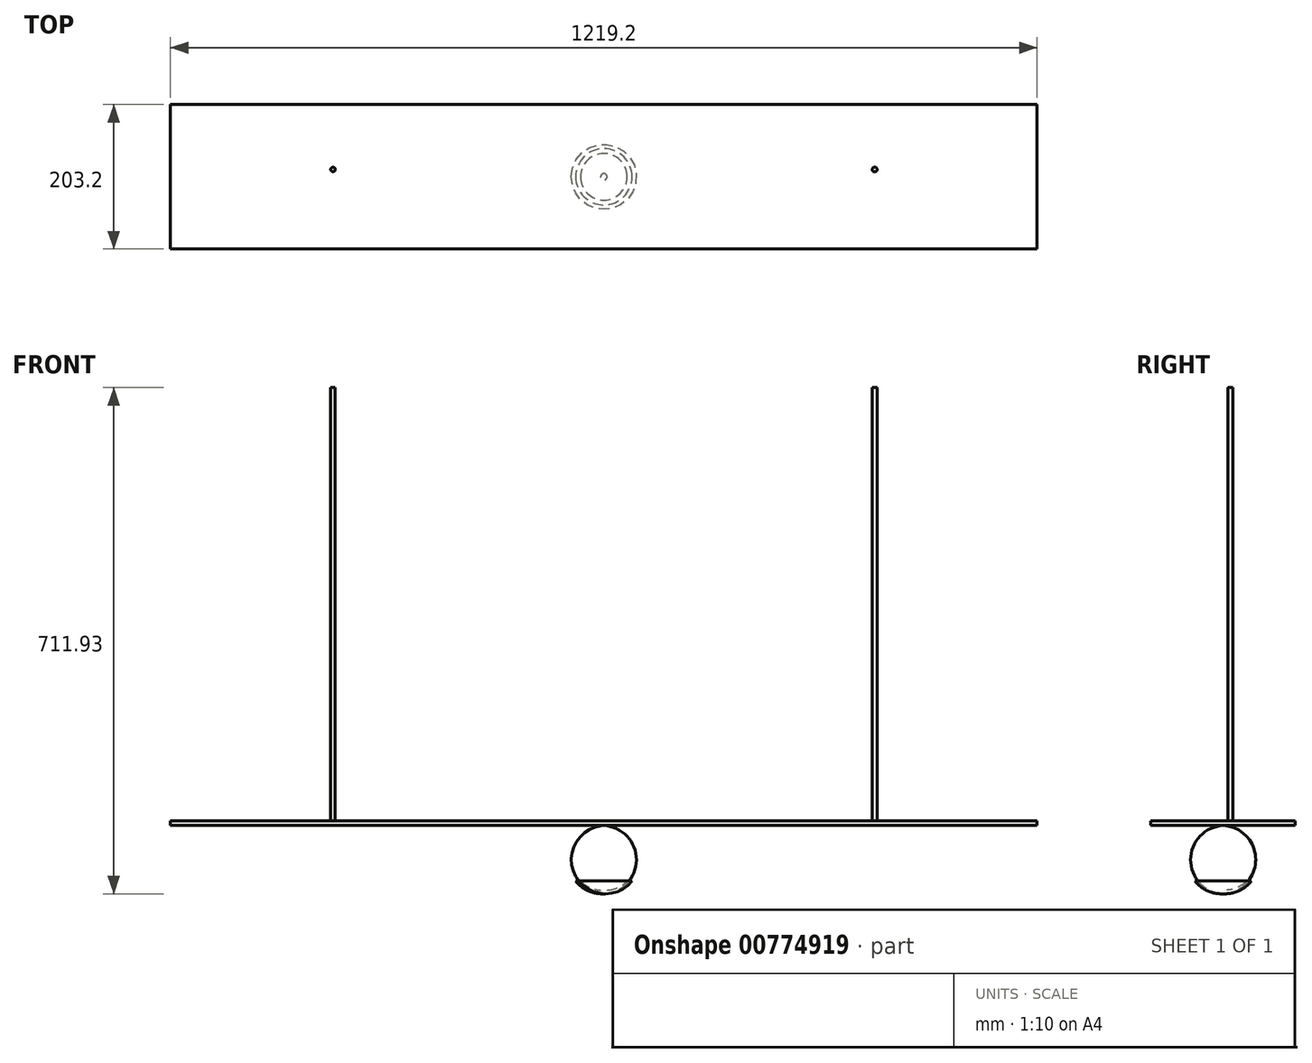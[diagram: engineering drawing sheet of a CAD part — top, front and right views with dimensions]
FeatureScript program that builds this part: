
annotation { "Feature Type Name" : "Feature", "Feature Type Description" : "" }
export const myFeature = defineFeature(function(context is Context, id is Id, definition is map)
    precondition{}
    {
        {
            var Q0;
            Q0=qCreatedBy(makeId("Top.planeOp"),FACE);
            var sketch = newSketch(context, id + "F0", { "sketchPlane" : qUnion([Q0])});
            skLineSegment(sketch, "E0.bottom", {"start": v(609.6, -101.6) * mm, "end": v(-609.6, -101.6) * mm});
            skLineSegment(sketch, "E0.top", {"start": v(609.6, 101.6) * mm, "end": v(-609.6, 101.6) * mm});
            skLineSegment(sketch, "E0.left", {"start": v(609.6, -101.6) * mm, "end": v(609.6, 101.6) * mm});
            skLineSegment(sketch, "E0.right", {"start": v(-609.6, -101.6) * mm, "end": v(-609.6, 101.6) * mm});
            skPoint(sketch, "E0.middle", {"position": v(0, 0) * mm});
            skSolve(sketch);
        }
        {
            var Q0;
            Q0=makeQuery(id+"F0.imprint","IMPRINT",FACE,{"disambiguationData":[TD([[makeQuery(id+"F0.imprint","IMPRINT",EDGE,{"derivedFrom":sQuery(id+"F0.wireOp",EDGE,"E0.bottom")}),-1.0]])]});
            extrude(context, id + "F1", {"entities" : qUnion([Q0]), "depth" : 6.35 * mm, "offsetDistance" : 25.4 * mm});
        }
        {
            var Q0;
            Q0=makeQuery(id+"F1.opExtrude","CAP_FACE",FACE,{"disambiguationData":[OSD([sQuery(id+"F0.wireOp",EDGE,"E0.bottom"),sQuery(id+"F0.wireOp",EDGE,"E0.top"),sQuery(id+"F0.wireOp",EDGE,"E0.left"),sQuery(id+"F0.wireOp",EDGE,"E0.right")])],"isStart":false});
            var sketch = newSketch(context, id + "F2", { "sketchPlane" : qUnion([Q0])});
            skCircle(sketch, "E1", {"center": v(-381, 10.37) * mm, "radius": 3.18 * mm});
            skCircle(sketch, "E2", {"center": v(381, 10.31) * mm, "radius": 3.4 * mm});
            skSolve(sketch);
        }
        {
            var Q0;
            Q0 = qSketchRegion(id + "F2", true);
            extrude(context, id + "F3", {"entities" : qUnion([Q0]), "operationType" : NewBodyOperationType.ADD, "depth" : 609.6 * mm, "offsetDistance" : 25.4 * mm});
        }
        {
            var Q0;
            Q0=qCreatedBy(makeId("Front.planeOp"),FACE);
            var sketch = newSketch(context, id + "F4", { "sketchPlane" : qUnion([Q0])});
            skArc(sketch, "E3", {"start": v(0, -95.93) * mm, "mid": v(50.27, -47.96) * mm, "end": v(0, 0) * mm});
            skPoint(sketch, "E3.first.point", {"position": v(0, 0) * mm});
            skPoint(sketch, "E3.second.point", {"position": v(0, -95.93) * mm});
            skPoint(sketch, "E3.third.point", {"position": v(-44.55, -58.68) * mm});
            skLineSegment(sketch, "E4", {"start": v(0, 0) * mm, "end": v(0, -95.93) * mm});
            skSolve(sketch);
        }
        {
            var Q0;
            Q0 = qSketchRegion(id + "F4", true);
            var Q1;
            Q1=sQuery(id+"F4.wireOp",EDGE,"E4");
            revolve(context, id + "F5", {"operationType" : NewBodyOperationType.ADD, "surfaceOperationType" : NewSurfaceOperationType.NEW, "entities" : qUnion([Q0]), "axis" : qUnion([Q1]), "revolveType" : RevolveType.FULL});
        }
        {
            var Q0;
            Q0=qCreatedBy(makeId("Front.planeOp"),FACE);
            var sketch = newSketch(context, id + "F6", { "sketchPlane" : qUnion([Q0])});
            skLineSegment(sketch, "E5.bottom", {"start": v(-68.22, -78.12) * mm, "end": v(75.87, -78.12) * mm});
            skLineSegment(sketch, "E5.top", {"start": v(-68.22, -143.84) * mm, "end": v(75.87, -143.84) * mm});
            skLineSegment(sketch, "E5.left", {"start": v(-68.22, -78.12) * mm, "end": v(-68.22, -143.84) * mm});
            skLineSegment(sketch, "E5.right", {"start": v(75.87, -78.12) * mm, "end": v(75.87, -143.84) * mm});
            skSolve(sketch);
        }
        {
            var Q0;
            Q0=makeQuery(id+"F6.imprint","IMPRINT",FACE,{"disambiguationData":[TD([[makeQuery(id+"F6.imprint","IMPRINT",EDGE,{"derivedFrom":sQuery(id+"F6.wireOp",EDGE,"E5.bottom")}),-1.0]])]});
            extrude(context, id + "F7", {"entities" : qUnion([Q0]), "operationType" : NewBodyOperationType.REMOVE, "oppositeDirection" : true, "depth" : 76.2 * mm, "offsetDistance" : 25.4 * mm, "hasSecondDirection" : true, "secondDirectionOppositeDirection" : false, "secondDirectionDepth" : 76.2 * mm});
        }
        {
            var Q0;
            Q0=makeQuery(id+"F7.boolean.opBoolean","COPY",FACE,{"derivedFrom":makeQuery(id+"F7.opExtrude","SWEPT_FACE",FACE,{"disambiguationData":[OSD([sQuery(id+"F6.wireOp",EDGE,"E5.bottom")])]})});
            shell(context, id + "F8", {"entities" : qUnion([Q0]), "thickness" : 5.08 * mm});
        }
    });
